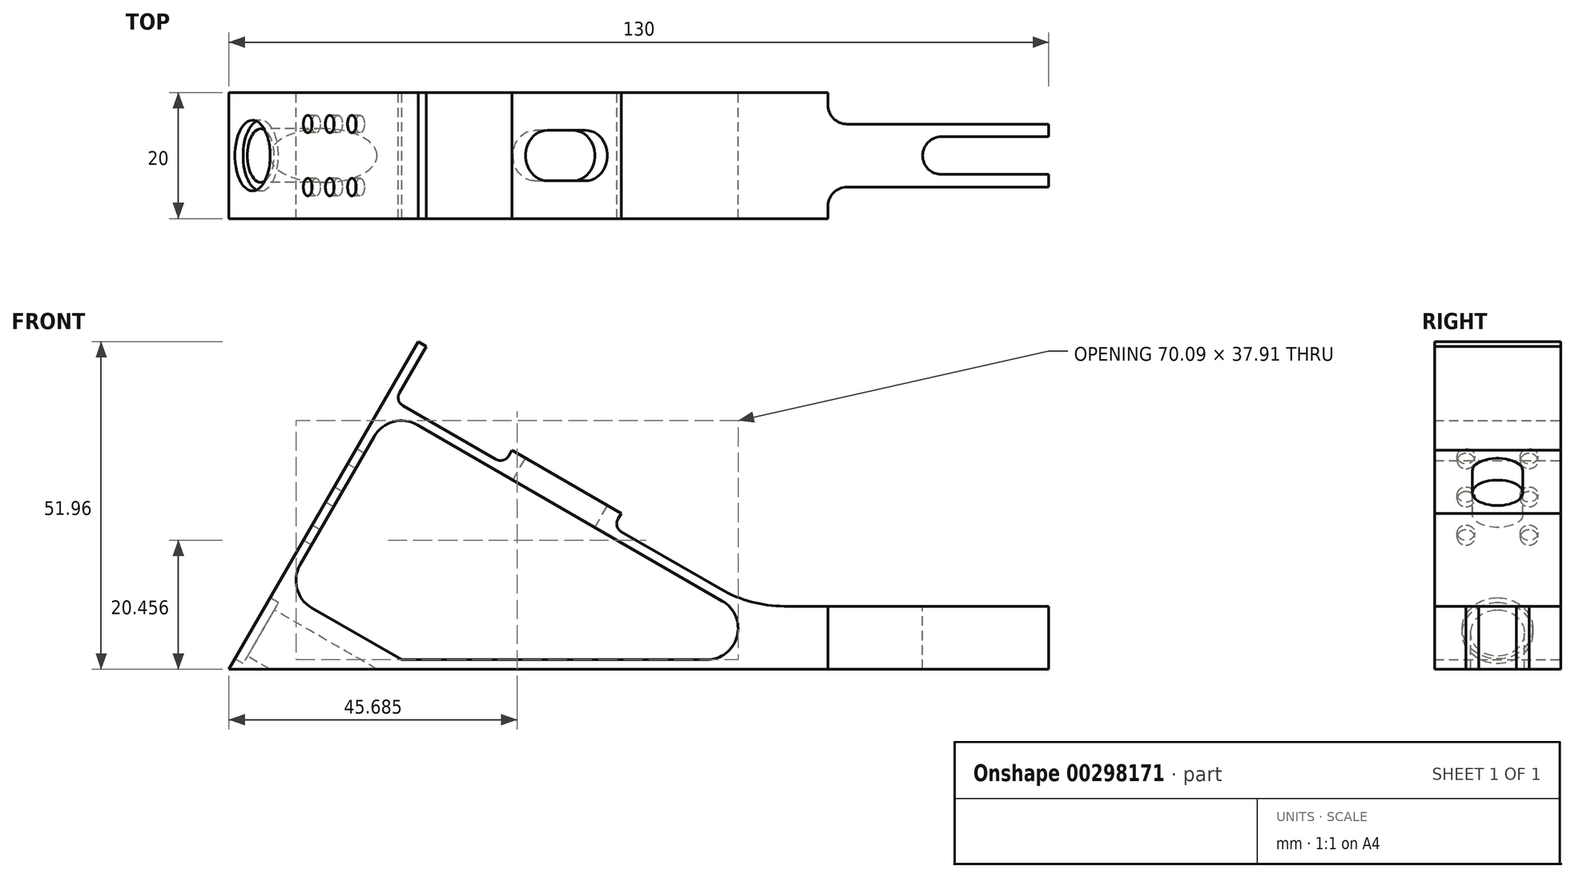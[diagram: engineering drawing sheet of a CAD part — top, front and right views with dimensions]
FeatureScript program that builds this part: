
annotation { "Feature Type Name" : "Feature", "Feature Type Description" : "" }
export const myFeature = defineFeature(function(context is Context, id is Id, definition is map)
    precondition{}
    {
        {
            var Q0;
            Q0=qCreatedBy(makeId("Front.planeOp"),FACE);
            var sketch = newSketch(context, id + "F0", { "sketchPlane" : qUnion([Q0])});
            skLineSegment(sketch, "E0", {"start": v(0, 0) * mm, "end": v(130, 0) * mm});
            skLineSegment(sketch, "E1", {"start": v(130, 0) * mm, "end": v(130, 10) * mm});
            skLineSegment(sketch, "E2", {"start": v(130, 10) * mm, "end": v(88.04, 10) * mm});
            skLineSegment(sketch, "E3", {"start": v(78.04, 12.68) * mm, "end": v(62.24, 21.8) * mm});
            skLineSegment(sketch, "E4", {"start": v(27.05, 43.85) * mm, "end": v(31.3, 51.21) * mm});
            skLineSegment(sketch, "E5", {"start": v(31.3, 51.21) * mm, "end": v(30, 51.96) * mm});
            skLineSegment(sketch, "E6", {"start": v(30, 51.96) * mm, "end": v(0, 0) * mm});
            skLineSegment(sketch, "E7", {"start": v(44.37, 33.85) * mm, "end": v(44.87, 34.72) * mm});
            skLineSegment(sketch, "E8", {"start": v(44.87, 34.72) * mm, "end": v(62.2, 24.72) * mm});
            skLineSegment(sketch, "E9", {"start": v(62.2, 24.72) * mm, "end": v(61.7, 23.85) * mm});
            skPoint(sketch, "E9.endSnap0", {"position": v(60.94, 22.55) * mm});
            skLineSegment(sketch, "E10.trimOffspring", {"start": v(42.32, 33.3) * mm, "end": v(27.6, 41.8) * mm});
            skPoint(sketch, "E11.visualSharp", {"position": v(26.3, 42.55) * mm});
            skArc(sketch, "E11.filletArc", {"start": v(27.05, 43.85) * mm, "mid": v(26.9, 42.71) * mm, "end": v(27.6, 41.8) * mm});
            skPoint(sketch, "E12.visualSharp", {"position": v(43.62, 32.55) * mm});
            skArc(sketch, "E12.filletArc", {"start": v(42.32, 33.3) * mm, "mid": v(43.46, 33.15) * mm, "end": v(44.37, 33.85) * mm});
            skArc(sketch, "E13.filletArc", {"start": v(61.7, 23.85) * mm, "mid": v(61.54, 22.71) * mm, "end": v(62.24, 21.8) * mm});
            skArc(sketch, "E14.filletArc", {"start": v(78.04, 12.68) * mm, "mid": v(82.86, 10.68) * mm, "end": v(88.04, 10) * mm});
            skLineSegment(sketch, "E15", {"start": v(13.13, 9.74) * mm, "end": v(27.4, 1.5) * mm});
            skLineSegment(sketch, "E16", {"start": v(27.4, 1.5) * mm, "end": v(75.74, 1.5) * mm});
            skLineSegment(sketch, "E17", {"start": v(78.24, 10.83) * mm, "end": v(29.88, 38.75) * mm});
            skLineSegment(sketch, "E18", {"start": v(23.05, 36.92) * mm, "end": v(11.3, 16.57) * mm});
            skPoint(sketch, "E19.visualSharp", {"position": v(94.4, 1.5) * mm});
            skArc(sketch, "E19.filletArc", {"start": v(75.74, 1.5) * mm, "mid": v(80.57, 5.2) * mm, "end": v(78.24, 10.83) * mm});
            skPoint(sketch, "E20.visualSharp", {"position": v(8.8, 12.24) * mm});
            skArc(sketch, "E20.filletArc", {"start": v(11.3, 16.57) * mm, "mid": v(10.8, 12.78) * mm, "end": v(13.13, 9.74) * mm});
            skPoint(sketch, "E21.visualSharp", {"position": v(25.55, 41.25) * mm});
            skArc(sketch, "E21.filletArc", {"start": v(29.88, 38.75) * mm, "mid": v(26.09, 39.25) * mm, "end": v(23.05, 36.92) * mm});
            skSolve(sketch);
        }
        {
            var Q0;
            Q0 = qSketchRegion(id + "F0", true);
            extrude(context, id + "F1", {"entities" : qUnion([Q0]), "endBound" : BoundingType.SYMMETRIC, "depth" : 20 * mm});
        }
        {
            var Q0;
            Q0=makeQuery(id+"F1.opExtrude","SWEPT_FACE",FACE,{"disambiguationData":[OSD([sQuery(id+"F0.wireOp",EDGE,"E2")])]});
            var sketch = newSketch(context, id + "F2", { "sketchPlane" : qUnion([Q0])});
            skArc(sketch, "E22", {"start": v(113, 3) * mm, "mid": v(110, 0) * mm, "end": v(113, -3) * mm});
            skPoint(sketch, "E22.centerSnap0", {"position": v(88.04, 0) * mm});
            skLineSegment(sketch, "E23", {"start": v(113, 3) * mm, "end": v(130, 3) * mm});
            skLineSegment(sketch, "E24", {"start": v(130, 3) * mm, "end": v(130, -3) * mm});
            skLineSegment(sketch, "E25", {"start": v(130, -3) * mm, "end": v(113, -3) * mm});
            skLineSegment(sketch, "E26", {"start": v(130, 5) * mm, "end": v(98, 5) * mm});
            skLineSegment(sketch, "E27", {"start": v(95, 8) * mm, "end": v(95, 10) * mm});
            skLineSegment(sketch, "E28", {"start": v(95, 10) * mm, "end": v(130, 10) * mm});
            skLineSegment(sketch, "E29", {"start": v(130, 10) * mm, "end": v(130, 5) * mm});
            skLineSegment(sketch, "E30", {"start": v(130, -10) * mm, "end": v(95, -10) * mm});
            skLineSegment(sketch, "E31", {"start": v(95, -10) * mm, "end": v(95, -8) * mm});
            skLineSegment(sketch, "E32", {"start": v(98, -5) * mm, "end": v(130, -5) * mm});
            skLineSegment(sketch, "E33", {"start": v(130, -5) * mm, "end": v(130, -10) * mm});
            skPoint(sketch, "E34.visualSharp", {"position": v(95, 5) * mm});
            skArc(sketch, "E34.filletArc", {"start": v(95, 8) * mm, "mid": v(95.88, 5.88) * mm, "end": v(98, 5) * mm});
            skPoint(sketch, "E35.visualSharp", {"position": v(95, -5) * mm});
            skArc(sketch, "E35.filletArc", {"start": v(98, -5) * mm, "mid": v(95.88, -5.88) * mm, "end": v(95, -8) * mm});
            skSolve(sketch);
        }
        {
            var Q0;
            Q0 = qSketchRegion(id + "F2", true);
            extrude(context, id + "F3", {"entities" : qUnion([Q0]), "operationType" : NewBodyOperationType.REMOVE, "endBound" : BoundingType.THROUGH_ALL, "oppositeDirection" : true, "depth" : 25 * mm});
        }
        {
            var Q0;
            Q0=makeQuery(id+"F1.opExtrude","SWEPT_FACE",FACE,{"disambiguationData":[OSD([sQuery(id+"F0.wireOp",EDGE,"E5")])]});
            var sketch = newSketch(context, id + "F4", { "sketchPlane" : qUnion([Q0])});
            skArc(sketch, "E36", {"start": v(28, -4) * mm, "mid": v(24, 0) * mm, "end": v(28, 4) * mm});
            skArc(sketch, "E37", {"start": v(35, -4) * mm, "mid": v(39, 0) * mm, "end": v(35, 4) * mm});
            skPoint(sketch, "E37.centerSnap0", {"position": v(1.5, 0) * mm});
            skLineSegment(sketch, "E38", {"start": v(35, -4) * mm, "end": v(28, -4) * mm});
            skLineSegment(sketch, "E39", {"start": v(28, 4) * mm, "end": v(35, 4) * mm});
            skSolve(sketch);
        }
        {
            var Q0;
            Q0 = qSketchRegion(id + "F4", true);
            extrude(context, id + "F5", {"entities" : qUnion([Q0]), "operationType" : NewBodyOperationType.REMOVE, "oppositeDirection" : true, "depth" : 25 * mm});
        }
        {
            var Q0;
            Q0=makeQuery(id+"F1.opExtrude","SWEPT_FACE",FACE,{"disambiguationData":[OSD([sQuery(id+"F0.wireOp",EDGE,"E6")])]});
            var sketch = newSketch(context, id + "F6", { "sketchPlane" : qUnion([Q0])});
            skCircle(sketch, "E40", {"center": v(-5, 25) * mm, "radius": 1.4 * mm});
            skCircle(sketch, "E41.0.1.0", {"center": v(-5, 32) * mm, "radius": 1.4 * mm});
            skCircle(sketch, "E41.0.2.0", {"center": v(-5, 39) * mm, "radius": 1.4 * mm});
            skCircle(sketch, "E41.1.0.0", {"center": v(5, 25) * mm, "radius": 1.4 * mm});
            skCircle(sketch, "E41.1.1.0", {"center": v(5, 32) * mm, "radius": 1.4 * mm});
            skCircle(sketch, "E41.1.2.0", {"center": v(5, 39) * mm, "radius": 1.4 * mm});
            skLineSegment(sketch, "E41.direction1", {"start": v(-5, 25) * mm, "end": v(5, 25) * mm, "construction": true});
            skLineSegment(sketch, "E41.direction2", {"start": v(-5, 25) * mm, "end": v(-5, 32) * mm, "construction": true});
            skPoint(sketch, "E42", {"position": v(0, 25) * mm});
            skLineSegment(sketch, "E43", {"start": v(0, 0) * mm, "end": v(0, 64.96) * mm, "construction": true});
            skPoint(sketch, "E43.endSnap0", {"position": v(0, 60) * mm});
            skSolve(sketch);
        }
        {
            var Q0;
            Q0 = qSketchRegion(id + "F6", true);
            extrude(context, id + "F7", {"entities" : qUnion([Q0]), "operationType" : NewBodyOperationType.REMOVE, "oppositeDirection" : true, "depth" : 25 * mm});
        }
        {
            var Q0;
            Q0=makeQuery(id+"F1.opExtrude","SWEPT_FACE",FACE,{"disambiguationData":[OSD([sQuery(id+"F0.wireOp",EDGE,"E6")])]});
            var sketch = newSketch(context, id + "F8", { "sketchPlane" : qUnion([Q0])});
            skCircle(sketch, "E44", {"center": v(0, 7.5) * mm, "radius": 5.6 * mm});
            skCircle(sketch, "E45", {"center": v(0, 7.5) * mm, "radius": 4.25 * mm});
            skSolve(sketch);
        }
        {
            var Q0;
            Q0=makeQuery(id+"F8.imprint","IMPRINT",FACE,{"disambiguationData":[TD([[makeQuery(id+"F8.imprint","IMPRINT",EDGE,{"derivedFrom":sQuery(id+"F8.wireOp",EDGE,"E45")}),1.0]])]});
            extrude(context, id + "F9", {"entities" : qUnion([Q0]), "operationType" : NewBodyOperationType.REMOVE, "endBound" : BoundingType.THROUGH_ALL, "oppositeDirection" : true, "depth" : 25 * mm});
        }
        {
            var Q0;
            Q0=makeQuery(id+"F8.imprint","IMPRINT",FACE,{"disambiguationData":[TD([[makeQuery(id+"F8.imprint","IMPRINT",EDGE,{"derivedFrom":sQuery(id+"F8.wireOp",EDGE,"E44")}),1.0]])]});
            extrude(context, id + "F10", {"entities" : qUnion([Q0]), "operationType" : NewBodyOperationType.REMOVE, "oppositeDirection" : true, "depth" : 1.5 * mm});
        }
    });
